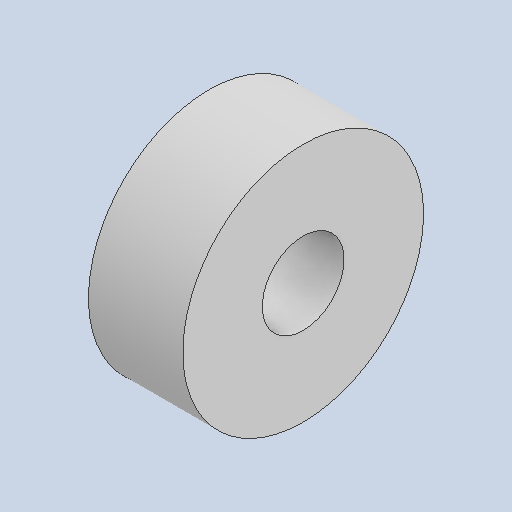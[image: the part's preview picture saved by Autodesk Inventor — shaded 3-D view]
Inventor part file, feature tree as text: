
AUTODESK INVENTOR PART (.ipt)
format: ipt  version: 2023 (Build 270158000, 158)  size: 134,656 bytes
history: native  units: in
note: dims shown in document units (in); Inventor stores cm internally (conversion verified against a paired STEP export)
features: extrude x1, sketch x1
ambient origin geometry x8: Origin, YZ Plane, XZ Plane, XY Plane, X Axis, Y Axis, Z Axis, Center Point
bodies: Solid1 (feature_tree)
feature tree (2):
  extrude  "Extrusion1"  Depth=0.196in
  sketch  "Sketch1"  dims[d0=0.5in d1=0.17in d2=0.196in d3=0.0in]
